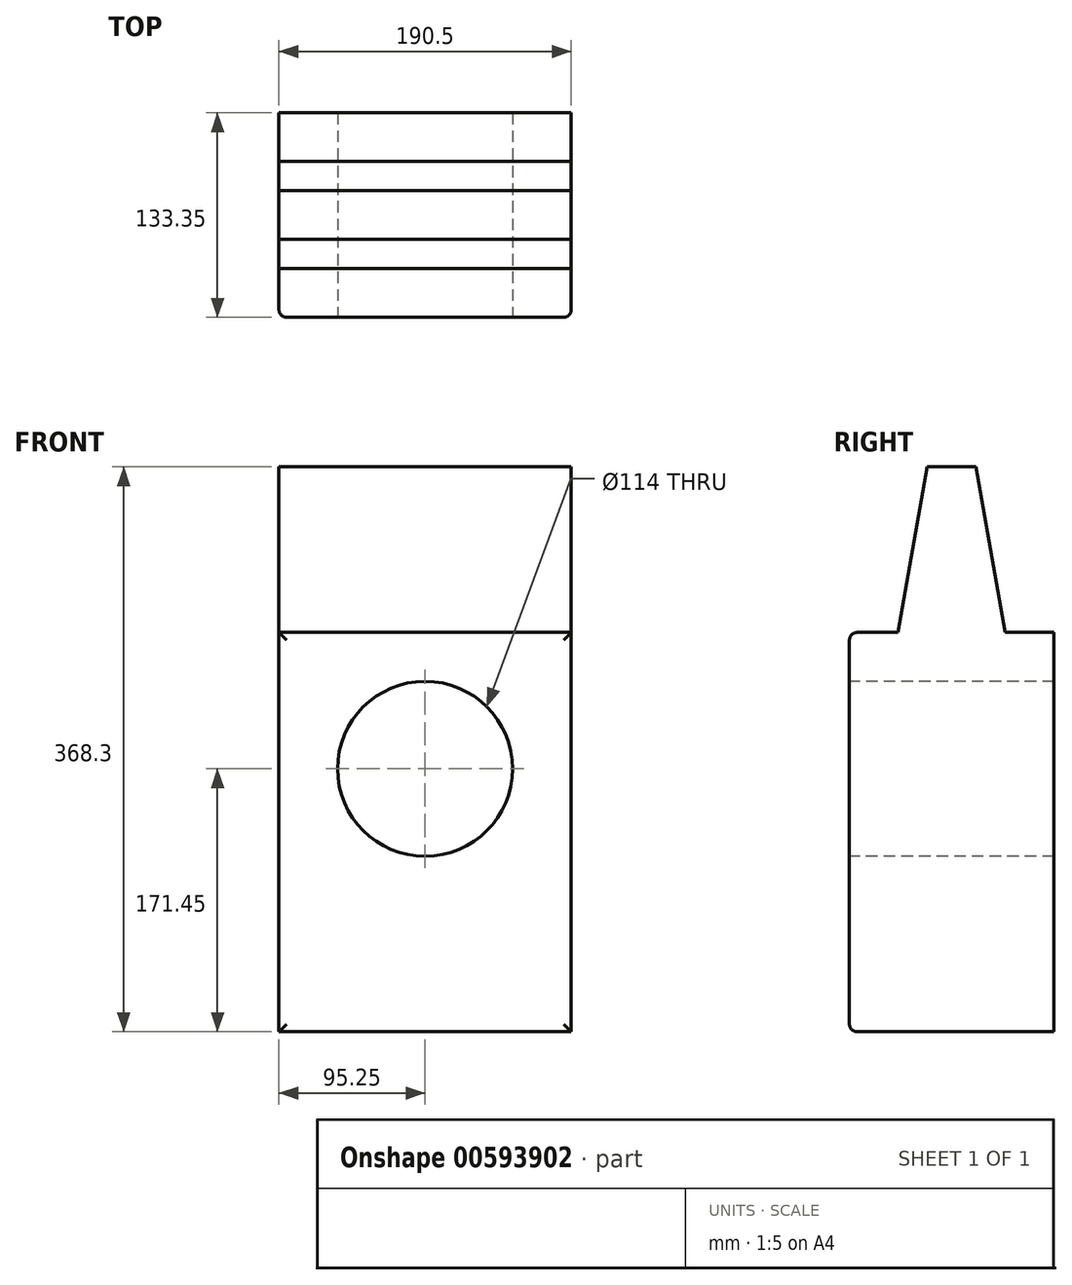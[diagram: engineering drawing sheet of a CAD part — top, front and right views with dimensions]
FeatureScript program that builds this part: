
annotation { "Feature Type Name" : "Feature", "Feature Type Description" : "" }
export const myFeature = defineFeature(function(context is Context, id is Id, definition is map)
    precondition{}
    {
        {
            var Q0;
            Q0=qCreatedBy(makeId("Right.planeOp"),FACE);
            var sketch = newSketch(context, id + "F0", { "sketchPlane" : qUnion([Q0])});
            skLineSegment(sketch, "E0.bottom", {"start": v(0, 0) * mm, "end": v(-133.35, 0) * mm});
            skLineSegment(sketch, "E0.top", {"start": v(0, 260.35) * mm, "end": v(-133.35, 260.35) * mm});
            skLineSegment(sketch, "E0.left", {"start": v(0, 0) * mm, "end": v(0, 260.35) * mm});
            skLineSegment(sketch, "E0.right", {"start": v(-133.35, 0) * mm, "end": v(-133.35, 260.35) * mm});
            skLineSegment(sketch, "E1", {"start": v(0, 260.35) * mm, "end": v(-31.75, 260.35) * mm});
            skLineSegment(sketch, "E2", {"start": v(-133.35, 260.35) * mm, "end": v(-101.6, 260.35) * mm});
            skLineSegment(sketch, "E3", {"start": v(-66.68, 260.35) * mm, "end": v(-66.68, 368.3) * mm});
            skLineSegment(sketch, "E4", {"start": v(-66.68, 368.3) * mm, "end": v(-82.55, 368.3) * mm});
            skLineSegment(sketch, "E5", {"start": v(-66.68, 368.3) * mm, "end": v(-50.8, 368.3) * mm});
            skLineSegment(sketch, "E6", {"start": v(-50.8, 368.3) * mm, "end": v(-31.75, 260.35) * mm});
            skLineSegment(sketch, "E7", {"start": v(-82.55, 368.3) * mm, "end": v(-101.6, 260.35) * mm});
            skSolve(sketch);
        }
        {
            var Q0;
            {var subQ0=sQuery(id+"F0.wireOp",EDGE,"E3");Q0=makeQuery(id+"F0.imprint","IMPRINT",FACE,{"disambiguationData":[TD([[makeQuery(id+"F0.imprint","IMPRINT",EDGE,{"derivedFrom":subQ0}),1.0]])]});}
            var Q1;
            {var subQ0=sQuery(id+"F0.wireOp",EDGE,"E3");Q1=makeQuery(id+"F0.imprint","IMPRINT",FACE,{"disambiguationData":[TD([[makeQuery(id+"F0.imprint","IMPRINT",EDGE,{"derivedFrom":subQ0}),-1.0]])]});}
            var Q2;
            Q2=makeQuery(id+"F0.imprint","IMPRINT",FACE,{"disambiguationData":[TD([[makeQuery(id+"F0.imprint","IMPRINT",EDGE,{"derivedFrom":sQuery(id+"F0.wireOp",EDGE,"E0.bottom")}),-1.0]])]});
            extrude(context, id + "F1", {"entities" : qUnion([Q0, Q1, Q2]), "depth" : 190.5 * mm, "offsetDistance" : 25 * mm});
        }
        {
            var Q0;
            Q0=makeQuery(id+"F1.opExtrude","SWEPT_FACE",FACE,{"disambiguationData":[OSD([sQuery(id+"F0.wireOp",EDGE,"E0.right")])]});
            var sketch = newSketch(context, id + "F2", { "sketchPlane" : qUnion([Q0])});
            skLineSegment(sketch, "E8", {"start": v(95.25, 260.35) * mm, "end": v(95.25, 228.6) * mm});
            skLineSegment(sketch, "E9", {"start": v(95.25, 228.6) * mm, "end": v(95.25, 171.45) * mm});
            skCircle(sketch, "E10", {"center": v(95.25, 171.45) * mm, "radius": 57.15 * mm});
            skLineSegment(sketch, "E11", {"start": v(95.25, 114.3) * mm, "end": v(95.25, 76.3) * mm});
            skLineSegment(sketch, "E12", {"start": v(95.25, 76.3) * mm, "end": v(57.25, 76.3) * mm});
            skLineSegment(sketch, "E13", {"start": v(95.25, 76.3) * mm, "end": v(133.25, 76.3) * mm});
            skLineSegment(sketch, "E14", {"start": v(57.25, 76.3) * mm, "end": v(57.25, 32.3) * mm});
            skLineSegment(sketch, "E15", {"start": v(57.25, 32.3) * mm, "end": v(133.25, 32.3) * mm});
            skLineSegment(sketch, "E16", {"start": v(133.25, 76.3) * mm, "end": v(133.25, 32.3) * mm});
            skSolve(sketch);
        }
        {
            var Q0;
            Q0=sQuery(id+"F2.wireOp",VERTEX,"E9.end");
            var Q1;
            Q1=makeQuery(id+"F1.opExtrude","SWEPT_BODY",BODY,{"disambiguationData":[OSD([sQuery(id+"F0.wireOp",EDGE,"E0.bottom"),sQuery(id+"F0.wireOp",EDGE,"E0.top"),sQuery(id+"F0.wireOp",EDGE,"E0.left"),sQuery(id+"F0.wireOp",EDGE,"E0.right"),sQuery(id+"F0.wireOp",EDGE,"E4"),sQuery(id+"F0.wireOp",EDGE,"E5"),sQuery(id+"F0.wireOp",EDGE,"E6"),sQuery(id+"F0.wireOp",EDGE,"E7")])]});
            hole(context, id + "F3", {"style" : HoleStyle.SIMPLE, "endStyle" : HoleEndStyle.THROUGH, "holeDiameter" : 114 * mm, "majorDiameter" : 5 * mm, "isTappedThrough" : true, "tappedDepth" : 12 * mm, "tapClearance" : 3, "locations" : qUnion([Q0]), "scope" : qUnion([Q1])});
        }
        {
            var Q0;
            Q0=makeQuery(id+"F2.imprint","IMPRINT",FACE,{"disambiguationData":[TD([[makeQuery(id+"F2.imprint","IMPRINT",EDGE,{"derivedFrom":sQuery(id+"F2.wireOp",EDGE,"E12")}),1.0]])]});
            extrude(context, id + "F4", {"entities" : qUnion([Q0]), "operationType" : NewBodyOperationType.ADD, "oppositeDirection" : true, "depth" : 2 * mm, "offsetDistance" : 25 * mm});
        }
        {
            var Q0;
            Q0=makeQuery(id+"F1.opExtrude","CAP_EDGE",EDGE,{"disambiguationData":[OSD([sQuery(id+"F0.wireOp",EDGE,"E0.right")])],"isStart":true});
            var Q1;
            Q1=makeQuery(id+"F1.opExtrude","SWEPT_EDGE",EDGE,{"disambiguationData":[OSD([sQuery(id+"F0.wireOp",EDGE,"E0.top"),sQuery(id+"F0.wireOp",EDGE,"E0.right")])]});
            var Q2;
            Q2=makeQuery(id+"F1.opExtrude","CAP_EDGE",EDGE,{"disambiguationData":[OSD([sQuery(id+"F0.wireOp",EDGE,"E0.right")])],"isStart":false});
            var Q3;
            Q3=makeQuery(id+"F1.opExtrude","SWEPT_EDGE",EDGE,{"disambiguationData":[OSD([sQuery(id+"F0.wireOp",EDGE,"E0.bottom"),sQuery(id+"F0.wireOp",EDGE,"E0.right")])]});
            fillet(context, id + "F5", {"entities" : qUnion([Q0, Q1, Q2, Q3]), "radius" : 5 * mm, "tangentPropagation" : true, "allowEdgeOverflow" : false});
        }
    });
